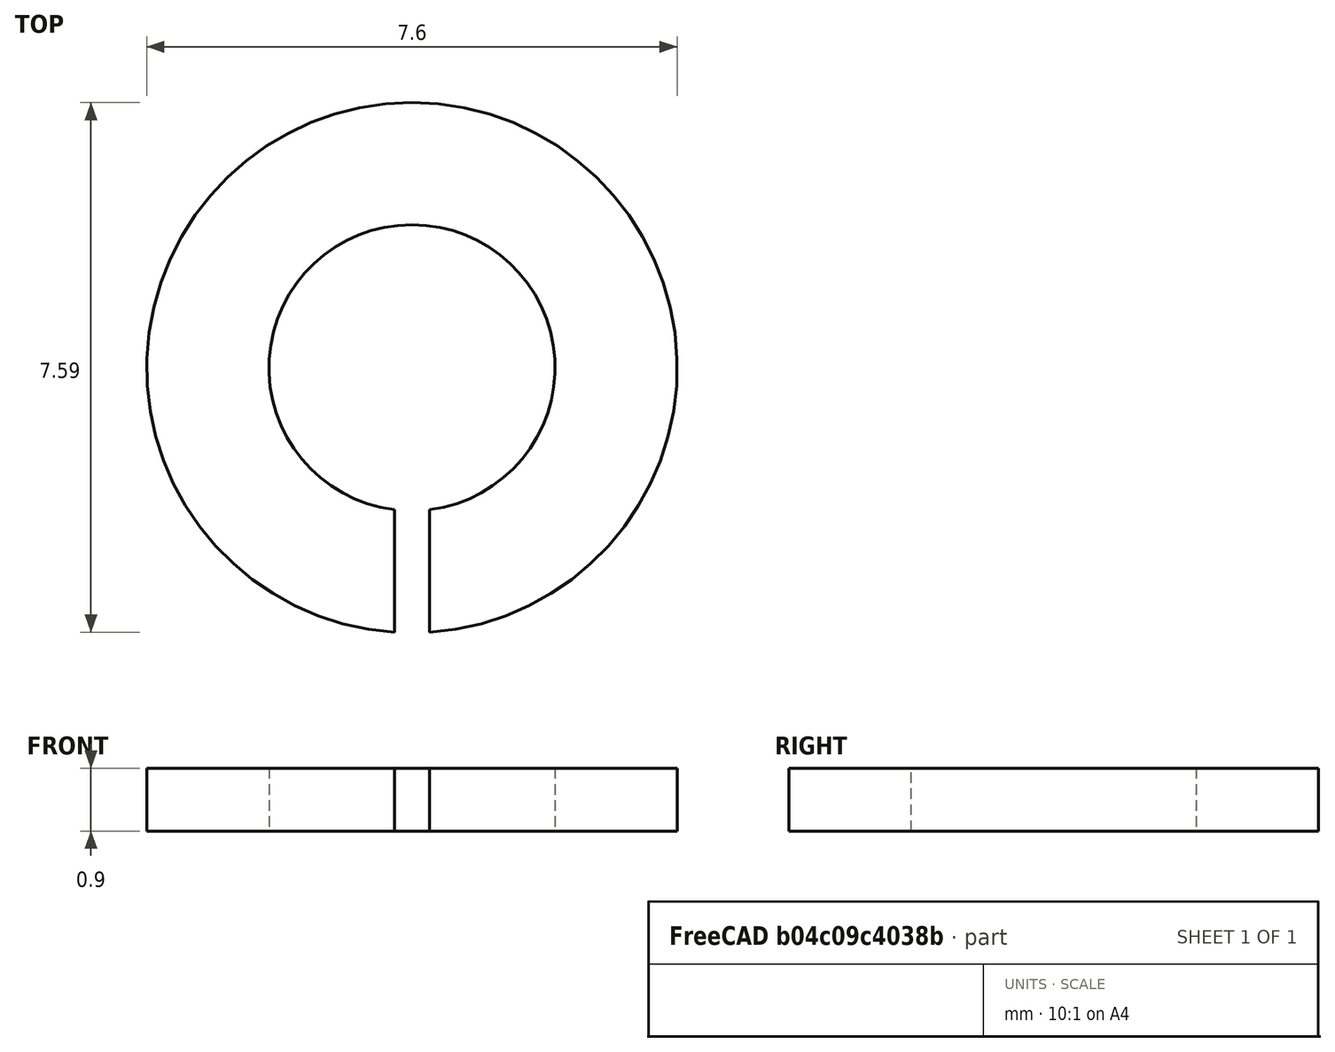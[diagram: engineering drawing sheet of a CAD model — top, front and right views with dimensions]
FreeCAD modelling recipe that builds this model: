
FCSTD DOCUMENT  (FreeCAD 0.15R4651 (Git))
Label: Federring_DIN127-B4
License: All rights reserved
LicenseURL: http://de.wikipedia.org/wiki/Alle_Rechte_vorbehalten
objects: Sketcher::SketchObject×1, PartDesign::Pad×1
note: 3 computed .brp shape members not serialized (recipe doc carries the construction recipe); baked Part::Feature solids carry a one-line shape summary decoded from their .brp

FEATURE [Sketcher::SketchObject] Sketch
  sketch-geometry (4):
    g0: ArcOfCircle CenterX=0 CenterY=0 CenterZ=0 NormalX=0 NormalY=0 NormalZ=1 Radius=2.05 StartAngle=4.83464 EndAngle=10.8733
    g1: ArcOfCircle CenterX=0 CenterY=0 CenterZ=0 NormalX=0 NormalY=0 NormalZ=1 Radius=3.8 StartAngle=4.77823 EndAngle=10.9297
    g2: LineSegment StartX=0.25 StartY=-2.0347 StartZ=0 EndX=0.25 EndY=-3.79177 EndZ=0
    g3: LineSegment StartX=-0.25 StartY=-3.79177 StartZ=0 EndX=-0.25 EndY=-2.0347 EndZ=0
  constraints (12):
    c: Coincident(g0,g-1)
    c: Coincident(g1,g-1)
    c: Vertical(g2)
    c: Vertical(g3)
    c: Coincident(g0,g2)
    c: Coincident(g0,g3)
    c: Coincident(g1,g2)
    c: Coincident(g1,g3)
    c: Symmetric(g1,g1,g-2)
    c: Radius(g0) = 2.05
    c: Radius(g1) = 3.8
    c: DistanceX(g1,g1) = -0.5
FEATURE [PartDesign::Pad] Pad  label="Federring DIN 127-B 4 #"
  Length = 0.9
  Length2 = 100
  Midplane = true
  Sketch = -> Sketch
  Type = 0
